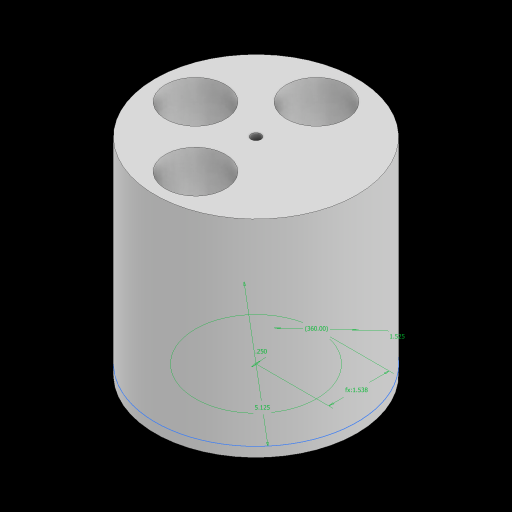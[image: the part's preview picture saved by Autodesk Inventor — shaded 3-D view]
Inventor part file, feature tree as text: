
AUTODESK INVENTOR PART (.ipt)
format: ipt  version: 2023 (Build 270158000, 158)  size: 129,536 bytes
history: native  units: in
note: dims shown in document units (in); Inventor stores cm internally (conversion verified against a paired STEP export)
features: sketch x2, extrude x2, plane x1
ambient origin geometry x8: Origin, YZ Plane, XZ Plane, XY Plane, X Axis, Y Axis, Z Axis, Center Point
bodies: Solid1 (feature_tree)
feature tree (5):
  sketch  "Sketch2"  dims[d2=5.125in d3=1.525in]
  extrude  "Extrusion1"  Depth=1.525in
  extrude  "Extrusion2"  Depth=2.5625in TaperAngle=360.0deg
  plane  "Work Plane1"
  sketch  "Sketch3"  dims[d5=1.5375in d6=1.5748in d8=360.0deg d10=5.0in d11=0.0in d12=0.25in d13=0.0in d14=0.25in d15=2.5625in d16=0.1in d17=1.0in]
